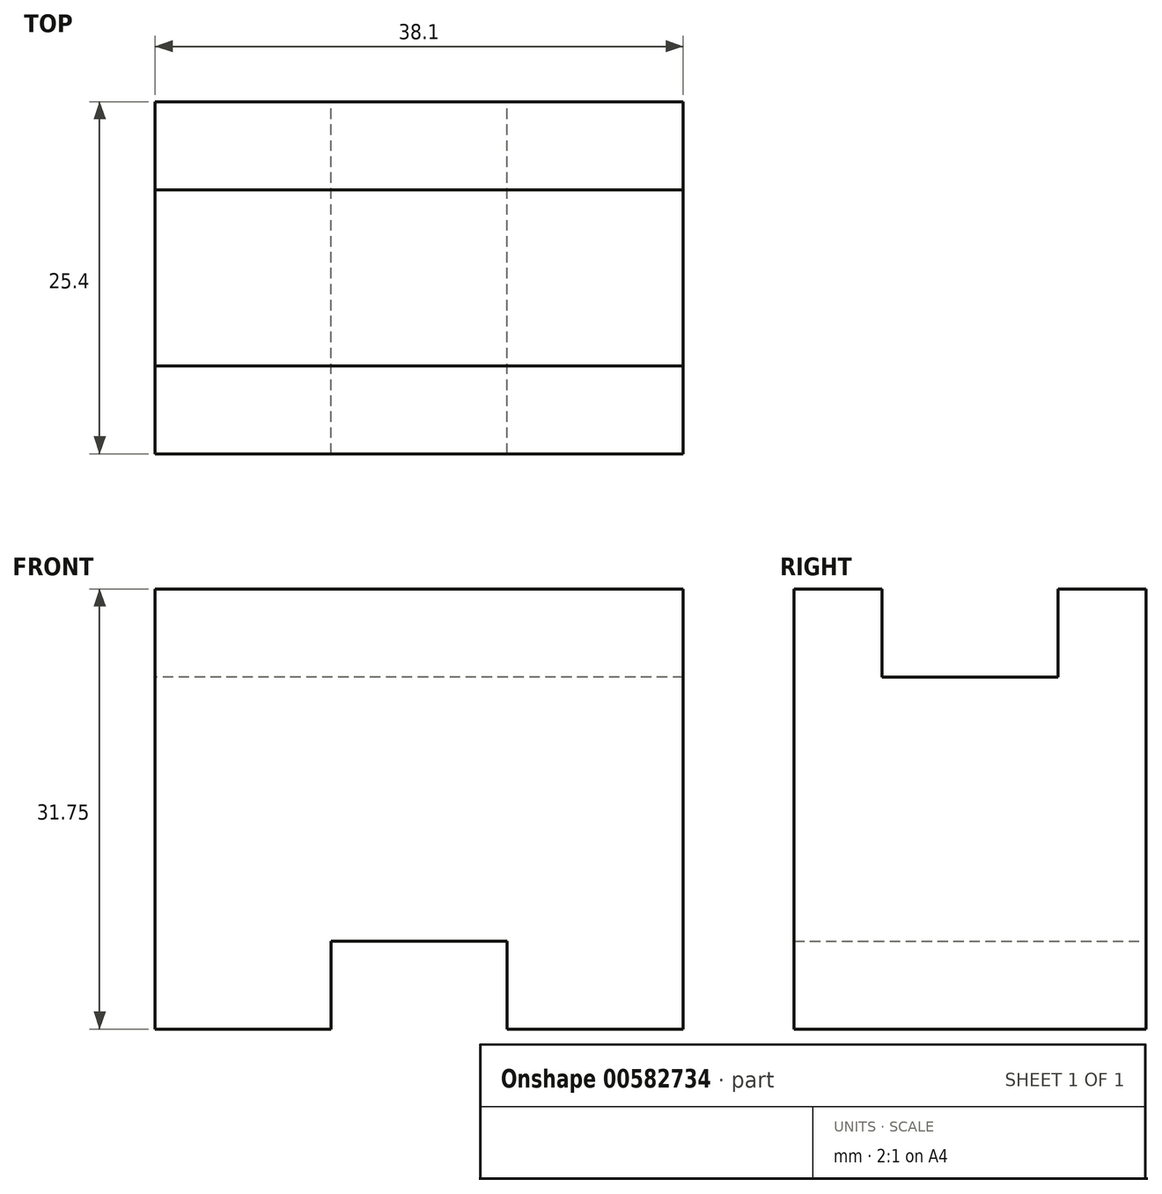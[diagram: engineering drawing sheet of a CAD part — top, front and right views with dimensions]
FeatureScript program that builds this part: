
annotation { "Feature Type Name" : "Feature", "Feature Type Description" : "" }
export const myFeature = defineFeature(function(context is Context, id is Id, definition is map)
    precondition{}
    {
        {
            var Q0;
            Q0=qCreatedBy(makeId("Front.planeOp"),FACE);
            var sketch = newSketch(context, id + "F0", { "sketchPlane" : qUnion([Q0])});
            skLineSegment(sketch, "E0", {"start": v(-39.37, 31.75) * mm, "end": v(-39.37, 0) * mm});
            skLineSegment(sketch, "E1", {"start": v(-39.37, 0) * mm, "end": v(-26.67, 0) * mm});
            skLineSegment(sketch, "E2", {"start": v(-26.67, 0) * mm, "end": v(-26.67, 6.35) * mm});
            skLineSegment(sketch, "E3", {"start": v(-26.67, 6.35) * mm, "end": v(-13.97, 6.35) * mm});
            skLineSegment(sketch, "E4", {"start": v(-13.97, 6.35) * mm, "end": v(-13.97, 0) * mm});
            skLineSegment(sketch, "E5", {"start": v(-13.97, 0) * mm, "end": v(-1.27, 0) * mm});
            skLineSegment(sketch, "E6", {"start": v(-1.27, 0) * mm, "end": v(-1.27, 31.75) * mm});
            skLineSegment(sketch, "E7", {"start": v(-1.27, 31.75) * mm, "end": v(-39.37, 31.75) * mm});
            skSolve(sketch);
        }
        {
            var Q0;
            Q0=makeQuery(id+"F0.imprint","IMPRINT",FACE,{"disambiguationData":[TD([[makeQuery(id+"F0.imprint","IMPRINT",EDGE,{"derivedFrom":sQuery(id+"F0.wireOp",EDGE,"E0")}),1.0]])]});
            var sketch = newSketch(context, id + "F1", { "sketchPlane" : qUnion([Q0])});
            skSolve(sketch);
        }
        {
            var Q0;
            Q0 = qSketchRegion(id + "F1", true);
            var Q1;
            Q1=makeQuery(id+"F0.imprint","IMPRINT",FACE,{"disambiguationData":[TD([[makeQuery(id+"F0.imprint","IMPRINT",EDGE,{"derivedFrom":sQuery(id+"F0.wireOp",EDGE,"E0")}),1.0]])]});
            extrude(context, id + "F2", {"entities" : qUnion([Q0, Q1]), "depth" : 25.4 * mm, "offsetDistance" : 25.4 * mm});
        }
        {
            var Q0;
            Q0=makeQuery(id+"F2.opExtrude","SWEPT_FACE",FACE,{"disambiguationData":[OSD([sQuery(id+"F0.wireOp",EDGE,"E0")])]});
            var sketch = newSketch(context, id + "F3", { "sketchPlane" : qUnion([Q0])});
            skLineSegment(sketch, "E8", {"start": v(6.35, 31.75) * mm, "end": v(6.35, 25.4) * mm});
            skLineSegment(sketch, "E9", {"start": v(6.35, 25.4) * mm, "end": v(19.05, 25.4) * mm});
            skLineSegment(sketch, "E10", {"start": v(19.05, 25.4) * mm, "end": v(19.05, 31.75) * mm});
            skSolve(sketch);
        }
        {
            var Q0;
            {var subQ0=sQuery(id+"F3.wireOp",EDGE,"E8");Q0=makeQuery(id+"F3.imprint","IMPRINT",FACE,{"disambiguationData":[TD([[makeQuery(id+"F3.imprint","IMPRINT",EDGE,{"derivedFrom":subQ0}),1.0]])]});}
            extrude(context, id + "F4", {"entities" : qUnion([Q0]), "operationType" : NewBodyOperationType.REMOVE, "oppositeDirection" : true, "depth" : 25.4 * mm, "offsetDistance" : 25.4 * mm});
        }
        {
            var Q0;
            Q0=makeQuery(id+"F4.boolean.opBoolean","COPY",FACE,{"derivedFrom":makeQuery(id+"F4.opExtrude","CAP_FACE",FACE,{"disambiguationData":[OSD([sQuery(id+"F0.wireOp",EDGE,"E0"),sQuery(id+"F0.wireOp",EDGE,"E7"),sQuery(id+"F3.wireOp",EDGE,"E8"),sQuery(id+"F3.wireOp",EDGE,"E9"),sQuery(id+"F3.wireOp",EDGE,"E10")])],"isStart":false})});
            extrude(context, id + "F5", {"entities" : qUnion([Q0]), "operationType" : NewBodyOperationType.REMOVE, "oppositeDirection" : true, "depth" : 25.4 * mm, "offsetDistance" : 25.4 * mm});
        }
    });
